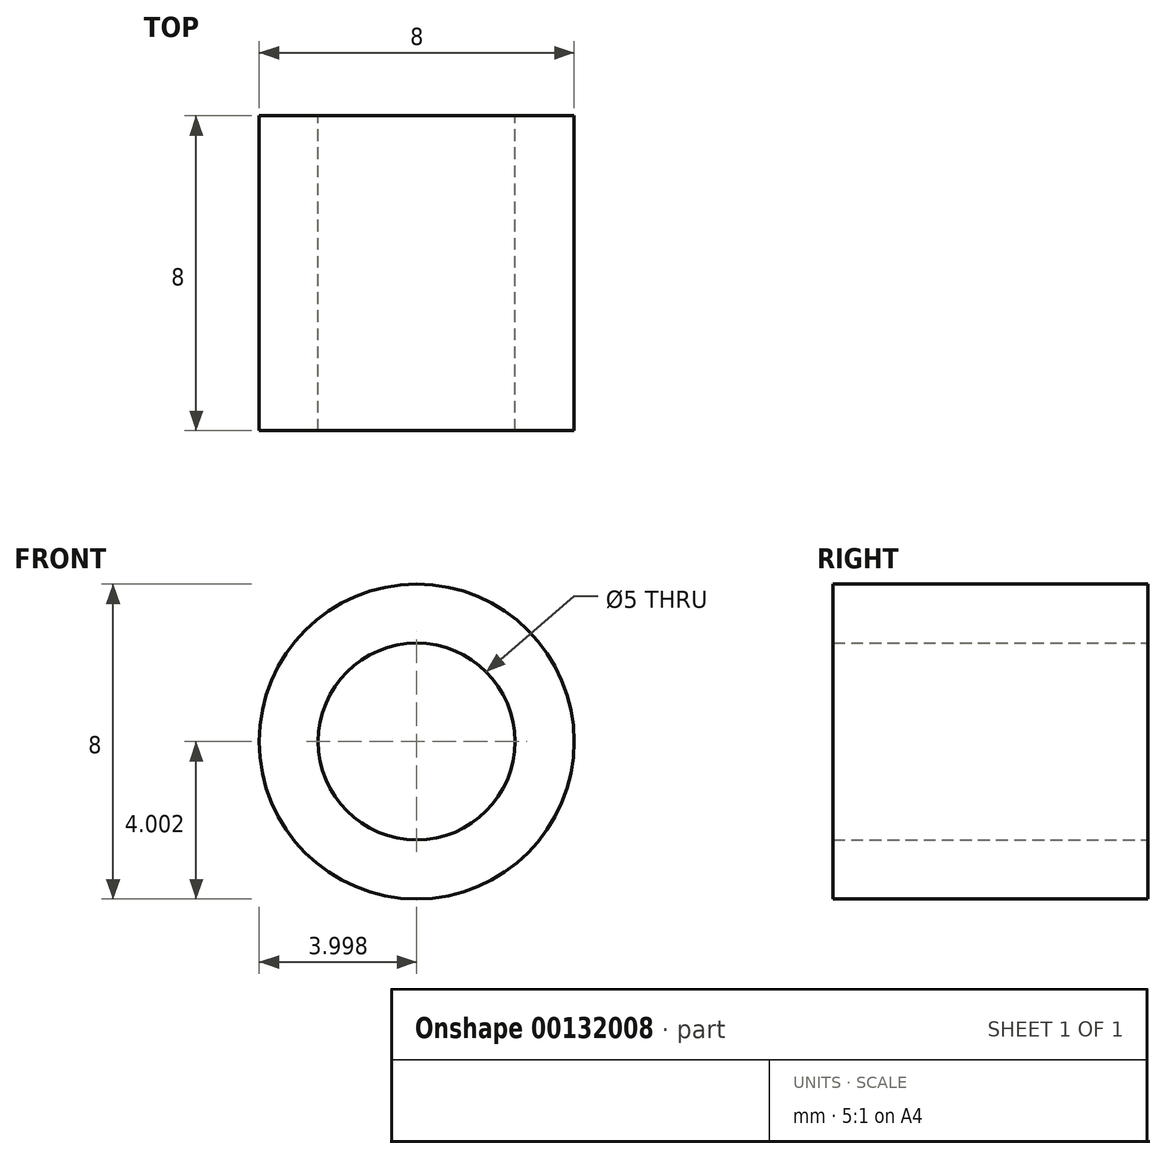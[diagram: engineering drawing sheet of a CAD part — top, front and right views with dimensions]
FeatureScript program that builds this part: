
annotation { "Feature Type Name" : "Feature", "Feature Type Description" : "" }
export const myFeature = defineFeature(function(context is Context, id is Id, definition is map)
    precondition{}
    {
        {
            var Q0;
            Q0=qCreatedBy(makeId("Front.planeOp"),FACE);
            var sketch = newSketch(context, id + "F0", { "sketchPlane" : qUnion([Q0])});
            skCircle(sketch, "E0", {"center": v(-90.22, 24.93) * mm, "radius": 2.5 * mm});
            skCircle(sketch, "E1", {"center": v(-90.22, 24.93) * mm, "radius": 4 * mm});
            skSolve(sketch);
        }
        {
            var Q0;
            Q0=makeQuery(id+"F0.imprint","IMPRINT",FACE,{"disambiguationData":[TD([[makeQuery(id+"F0.imprint","IMPRINT",EDGE,{"derivedFrom":sQuery(id+"F0.wireOp",EDGE,"E0")}),-1.0]])]});
            extrude(context, id + "F1", {"entities" : qUnion([Q0]), "depth" : 8 * mm});
        }
    });
